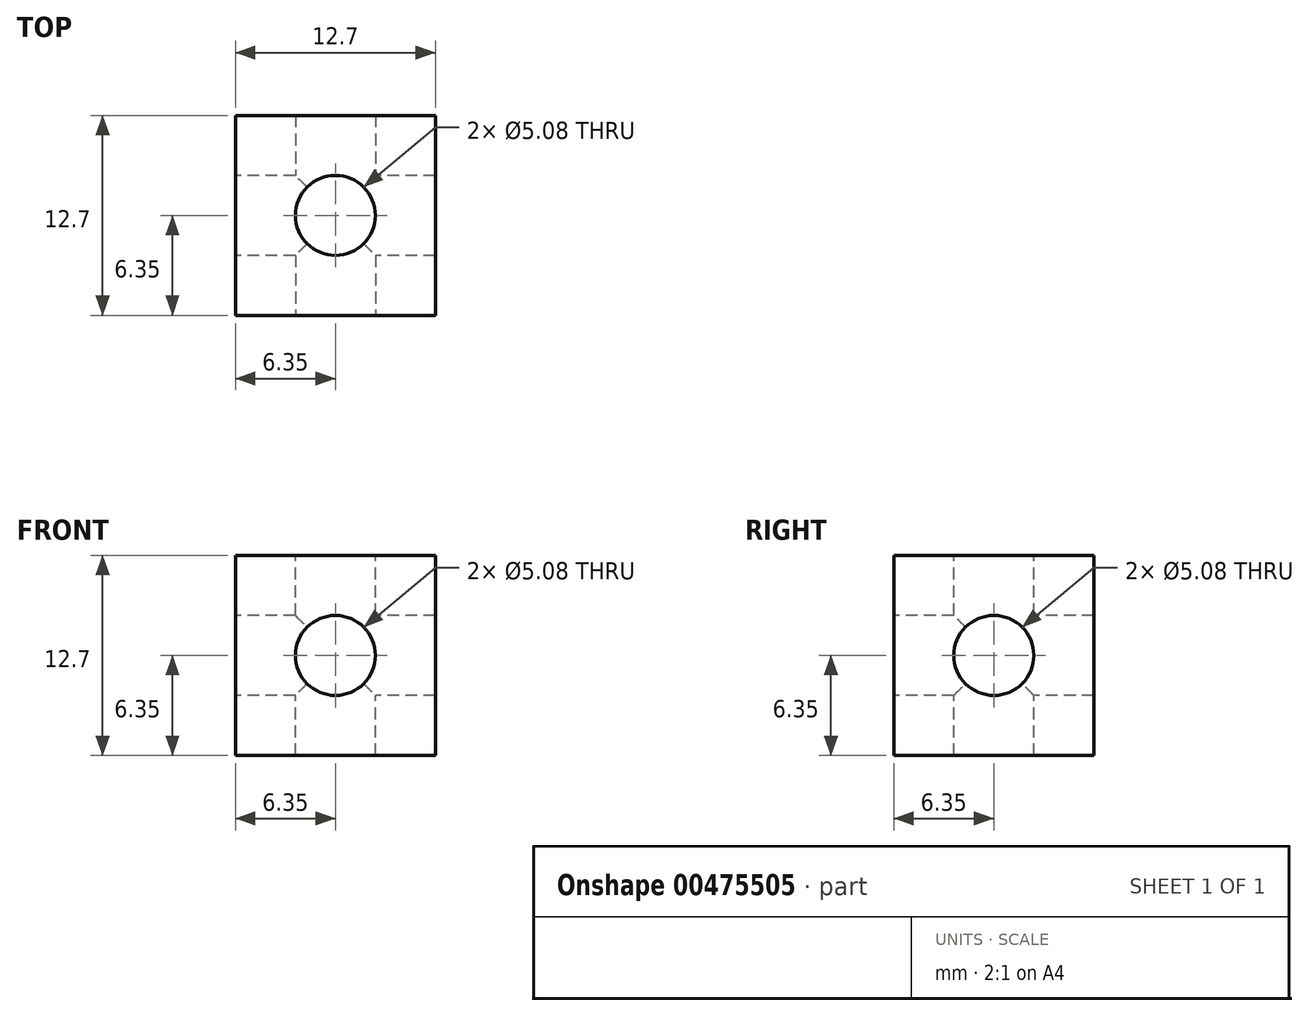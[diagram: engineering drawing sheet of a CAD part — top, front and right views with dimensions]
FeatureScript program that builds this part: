
annotation { "Feature Type Name" : "Feature", "Feature Type Description" : "" }
export const myFeature = defineFeature(function(context is Context, id is Id, definition is map)
    precondition{}
    {
        {
            var Q0;
            Q0=qCreatedBy(makeId("Top.planeOp"),FACE);
            var sketch = newSketch(context, id + "F0", { "sketchPlane" : qUnion([Q0])});
            skLineSegment(sketch, "E0.bottom", {"start": v(6.35, -6.35) * mm, "end": v(-6.35, -6.35) * mm});
            skLineSegment(sketch, "E0.top", {"start": v(6.35, 6.35) * mm, "end": v(-6.35, 6.35) * mm});
            skLineSegment(sketch, "E0.left", {"start": v(6.35, -6.35) * mm, "end": v(6.35, 6.35) * mm});
            skLineSegment(sketch, "E0.right", {"start": v(-6.35, -6.35) * mm, "end": v(-6.35, 6.35) * mm});
            skPoint(sketch, "E0.middle", {"position": v(0, 0) * mm});
            skSolve(sketch);
        }
        {
            var Q0;
            Q0 = qSketchRegion(id + "F0", true);
            extrude(context, id + "F1", {"entities" : qUnion([Q0]), "depth" : 12.7 * mm});
        }
        {
            var Q0;
            Q0=makeQuery(id+"F1.opExtrude","SWEPT_FACE",FACE,{"disambiguationData":[OSD([sQuery(id+"F0.wireOp",EDGE,"E0.bottom")])]});
            var sketch = newSketch(context, id + "F2", { "sketchPlane" : qUnion([Q0])});
            skCircle(sketch, "E1", {"center": v(0, 6.35) * mm, "radius": 2.54 * mm});
            skPoint(sketch, "E1.centerSnap0", {"position": v(6.35, 6.35) * mm});
            skSolve(sketch);
        }
        {
            var Q0;
            Q0 = qSketchRegion(id + "F2", true);
            extrude(context, id + "F3", {"entities" : qUnion([Q0]), "operationType" : NewBodyOperationType.REMOVE, "oppositeDirection" : true, "depth" : 25.4 * mm});
        }
        {
            var Q0;
            Q0=makeQuery(id+"F1.opExtrude","SWEPT_FACE",FACE,{"disambiguationData":[OSD([sQuery(id+"F0.wireOp",EDGE,"E0.right")])]});
            var sketch = newSketch(context, id + "F4", { "sketchPlane" : qUnion([Q0])});
            skCircle(sketch, "E2", {"center": v(0, 6.35) * mm, "radius": 2.54 * mm});
            skPoint(sketch, "E2.centerSnap0", {"position": v(6.35, 6.35) * mm});
            skSolve(sketch);
        }
        {
            var Q0;
            Q0 = qSketchRegion(id + "F4", true);
            extrude(context, id + "F5", {"entities" : qUnion([Q0]), "operationType" : NewBodyOperationType.REMOVE, "oppositeDirection" : true, "depth" : 25.4 * mm});
        }
        {
            var Q0;
            Q0=makeQuery(id+"F1.opExtrude","CAP_FACE",FACE,{"disambiguationData":[OSD([sQuery(id+"F0.wireOp",EDGE,"E0.bottom"),sQuery(id+"F0.wireOp",EDGE,"E0.top"),sQuery(id+"F0.wireOp",EDGE,"E0.left"),sQuery(id+"F0.wireOp",EDGE,"E0.right")])],"isStart":false});
            var sketch = newSketch(context, id + "F6", { "sketchPlane" : qUnion([Q0])});
            skCircle(sketch, "E3", {"center": v(0, 0) * mm, "radius": 2.54 * mm});
            skSolve(sketch);
        }
        {
            var Q0;
            Q0 = qSketchRegion(id + "F6", true);
            extrude(context, id + "F7", {"entities" : qUnion([Q0]), "operationType" : NewBodyOperationType.REMOVE, "oppositeDirection" : true, "depth" : 25.4 * mm});
        }
    });
